FREECAD ASSEMBLY — COMPONENT RECIPES ("Assembly")

This assembly document has 6 components, labeled P0..P5 below (a component is one placed body or linked part). 0 of them carry a construction recipe — the FreeCAD feature program that regenerates the part from scratch, quoted from this document or its linked companion documents; the rest are supplied as boundary geometry only. No exploded tour is included for this assembly.
COMPONENT P0 — geometry summary ("Body"; no construction recipe available for this part):
  bounding box: 62.0 x 62.0 x 38.0 mm
  tessellated surface: 8,284 triangles
  volume: 75779 mm^3 (52% of its bounding box)
COMPONENT P1 — geometry summary ("Body001"; no construction recipe available for this part):
  bounding box: 62.0 x 62.0 x 42.0 mm
  tessellated surface: 6,652 triangles
  volume: 59416 mm^3 (37% of its bounding box)
COMPONENT P2 — geometry summary ("Body002"; no construction recipe available for this part):
  bounding box: 106.5 x 45.0 x 45.0 mm
  tessellated surface: 19,208 triangles
  volume: 107142 mm^3 (50% of its bounding box)
  symmetry: revolution-symmetric about the z axis through its bounding-box center; mirror-symmetric across its y mid-plane
COMPONENT P3 — geometry summary ("GT-2-20"; no construction recipe available for this part):
  bounding box: 12.4 x 12.4 x 10.0 mm
  tessellated surface: 2,140 triangles
  volume: 881 mm^3 (57% of its bounding box)
  symmetry: 2-fold rotationally symmetric about the x axis; 4-fold rotationally symmetric about the z axis; mirror-symmetric across its y mid-plane, z mid-plane
COMPONENT P4 — geometry summary ("V-slot base"; no construction recipe available for this part):
  bounding box: 400.0 x 20.0 x 20.0 mm
  tessellated surface: 656 triangles
  volume: 72857 mm^3 (46% of its bounding box)
  symmetry: 2-fold rotationally symmetric about the x axis; 2-fold rotationally symmetric about the y axis; 4-fold rotationally symmetric about the z axis; mirror-symmetric across its x mid-plane, y mid-plane, z mid-plane
COMPONENT P5 — geometry summary ("17HS4401S Stepper Motor"; no construction recipe available for this part):
  bounding box: 60.8 x 47.8 x 42.0 mm
  tessellated surface: 68,854 triangles
  volume: 62586 mm^3 (51% of its bounding box)
PROVENANCE & LICENSES
A FreeCAD (.FCStd) document from a public repository crawl; recipes are the document's own serialized feature recipes (and, for linked parts, companion documents' recipes).
License: other.
